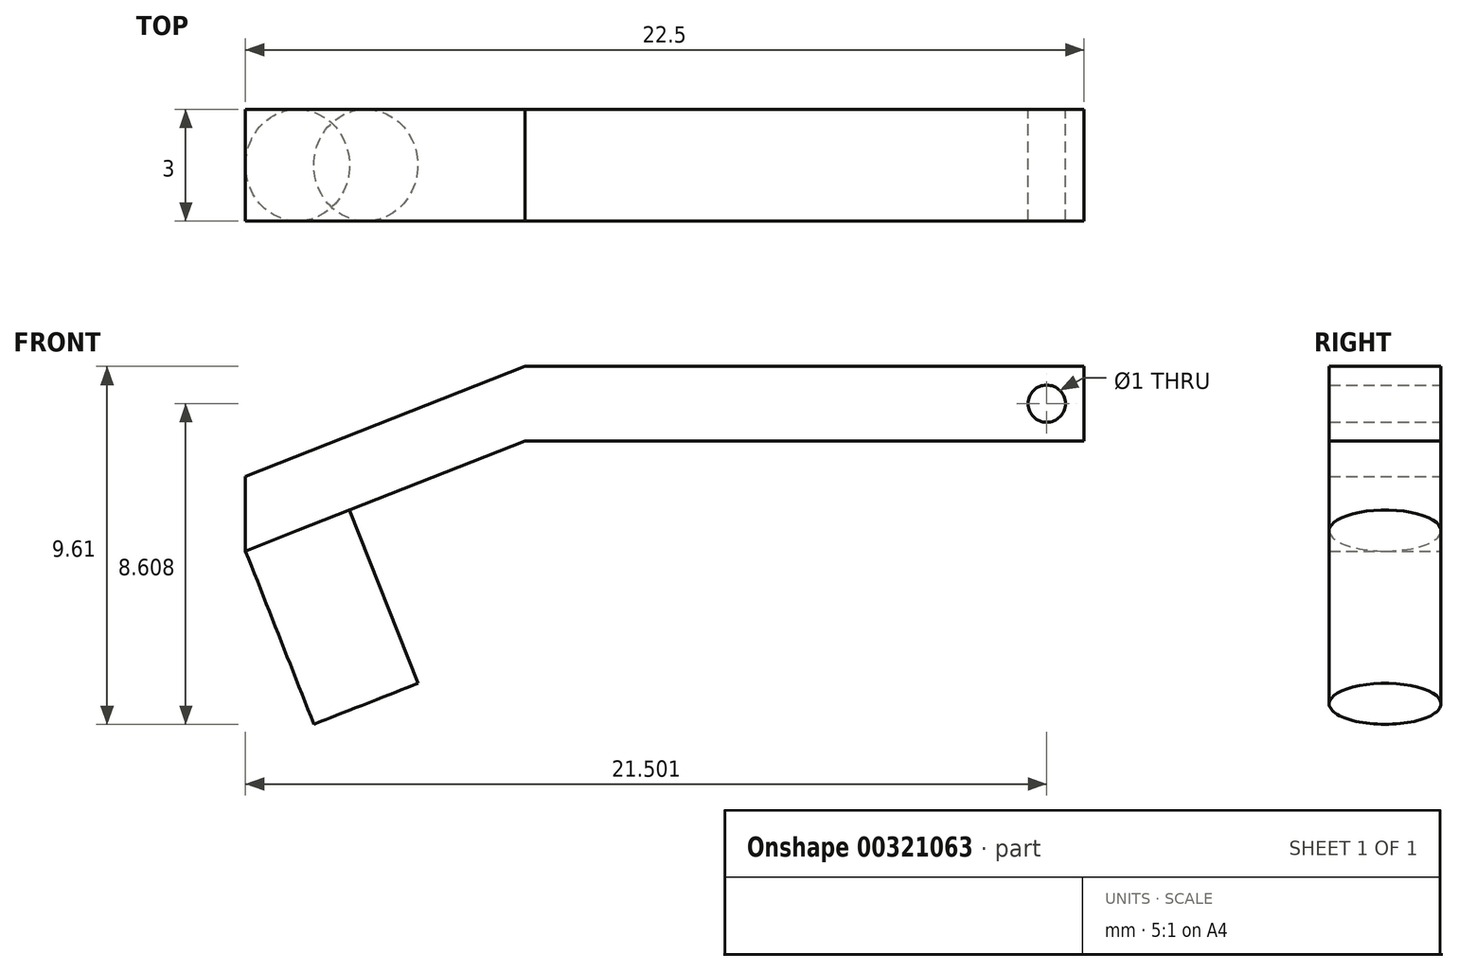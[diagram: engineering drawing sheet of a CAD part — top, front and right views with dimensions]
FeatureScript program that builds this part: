
annotation { "Feature Type Name" : "Feature", "Feature Type Description" : "" }
export const myFeature = defineFeature(function(context is Context, id is Id, definition is map)
    precondition{}
    {
        {
            var Q0;
            Q0=qCreatedBy(makeId("Front.planeOp"),FACE);
            var sketch = newSketch(context, id + "F0", { "sketchPlane" : qUnion([Q0])});
            skLineSegment(sketch, "E0.bottom", {"start": v(6.1, 15.32) * mm, "end": v(-8.9, 15.32) * mm});
            skLineSegment(sketch, "E0.top", {"start": v(6.1, 13.32) * mm, "end": v(-8.9, 13.32) * mm});
            skLineSegment(sketch, "E0.left", {"start": v(6.1, 15.32) * mm, "end": v(6.1, 13.32) * mm});
            skLineSegment(sketch, "E0.right", {"start": v(-8.9, 15.32) * mm, "end": v(-8.9, 13.32) * mm});
            skLineSegment(sketch, "E1", {"start": v(-8.9, 15.32) * mm, "end": v(-16.4, 12.36) * mm});
            skLineSegment(sketch, "E2", {"start": v(-16.4, 12.36) * mm, "end": v(-16.4, 10.36) * mm});
            skLineSegment(sketch, "E3", {"start": v(-16.4, 10.36) * mm, "end": v(-8.9, 13.32) * mm});
            skCircle(sketch, "E4", {"center": v(5.1, 14.32) * mm, "radius": 0.5 * mm});
            skSolve(sketch);
        }
        {
            var Q0;
            Q0 = qSketchRegion(id + "F0", true);
            extrude(context, id + "F1", {"entities" : qUnion([Q0]), "depth" : 3 * mm});
        }
        {
            var Q0;
            Q0=makeQuery(id+"F1.opExtrude","SWEPT_FACE",FACE,{"disambiguationData":[OSD([sQuery(id+"F0.wireOp",EDGE,"E3")])]});
            var sketch = newSketch(context, id + "F2", { "sketchPlane" : qUnion([Q0])});
            skCircle(sketch, "E5", {"center": v(-9.97, 1.5) * mm, "radius": 1.5 * mm});
            skSolve(sketch);
        }
        {
            var Q0;
            Q0 = qSketchRegion(id + "F2", true);
            extrude(context, id + "F3", {"entities" : qUnion([Q0]), "operationType" : NewBodyOperationType.ADD, "depth" : 5 * mm});
        }
    });
